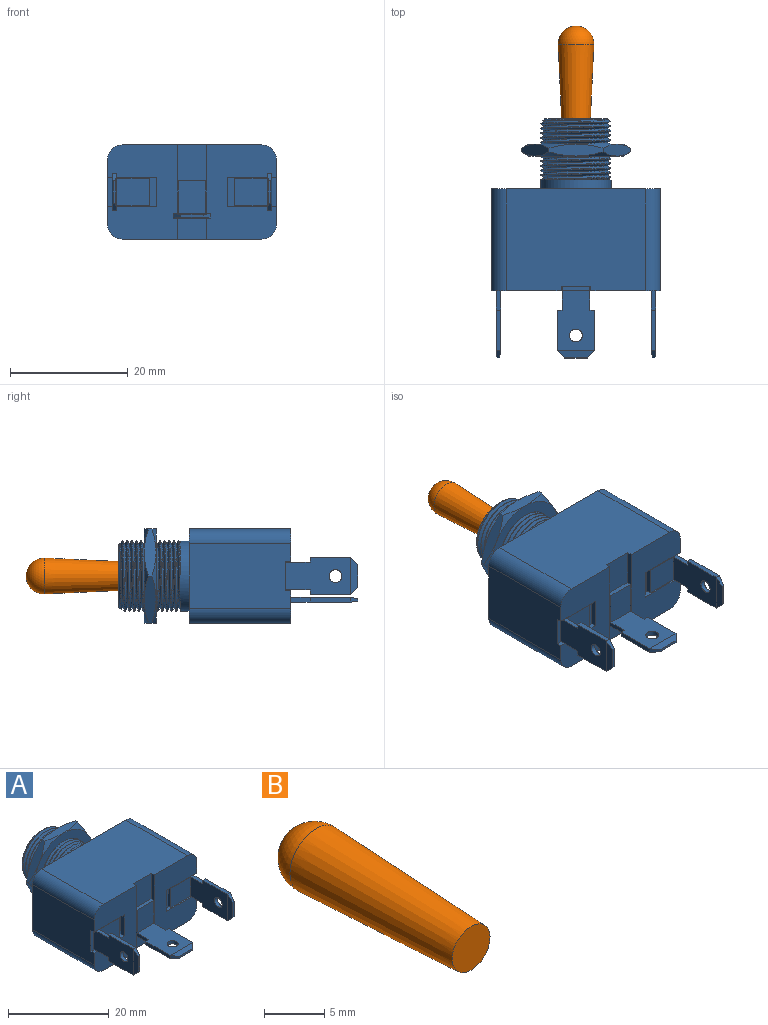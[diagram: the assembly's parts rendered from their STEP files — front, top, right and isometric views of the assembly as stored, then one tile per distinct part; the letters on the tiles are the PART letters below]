
ASSEMBLY  parts=2 mates=1
PART A: 155 faces, bbox 29.5x41.7x19.2 mm
  f0: cylinder r=5.95mm len=11.87mm, axis (0,1,0), area 2.4mm2, adj f6,f10,f12,f87
  f1: cylinder r=5.95mm len=0.9mm, axis (0,1,0), area 0mm2, adj f4,f11,f80
  f2: cylinder r=5.95mm len=11.91mm, axis (0,1,0), area 3.5mm2, adj f7,f11,f12,f36,f80
  f3: cylinder r=5.44mm len=4.26mm, axis (0,-1,0), area 0.4mm2, adj f5,f8,f11,f80
  f4: bspline ~11.99x11.99mm, area 11.2mm2, adj f1,f11,f12,f25,f80
  f5: bspline ~4.24x2.15mm, area 0mm2, adj f3,f11,f80
  f6: bspline ~11.99x11.99mm, area 15.3mm2, adj f0,f12,f26,f87
  f7: bspline ~11.99x11.99mm, area 20.1mm2, adj f2,f11,f12,f25,f80
  f8: bspline ~6x6mm, area 1.1mm2, adj f3,f11,f80
  f9: bspline ~11.99x11.99mm, area 5.4mm2, adj f12,f26,f87
  f10: bspline ~11.99x11.99mm, area 19.6mm2, adj f0,f11,f12,f27,f87
  f11: plane 10.42x0.95mm, normal (0,0,-1), area 6.8mm2, adj f1,f2,f3,f4,f5,f7,f8,f10
  f12: plane 10.42x0.95mm, normal (0,0,1), area 6.8mm2, adj f0,f2,f4,f6,f7,f9,f10,f14
  f13: cylinder r=5.95mm len=11.91mm, axis (0,1,0), area 59mm2, adj f11,f41,f50,f58,f67
  f14: cylinder r=5.95mm len=11.91mm, axis (0,1,0), area 3.5mm2, adj f11,f12,f40,f49
  f15: cylinder r=5.95mm len=11.91mm, axis (0,1,0), area 3.5mm2, adj f11,f12,f39,f48
  f16: cylinder r=5.95mm len=11.91mm, axis (0,1,0), area 3.5mm2, adj f11,f12,f38,f47
  f17: cylinder r=5.95mm len=11.91mm, axis (0,1,0), area 3.5mm2, adj f11,f12,f37,f46
  f18: cylinder r=5.95mm len=11.91mm, axis (0,1,0), area 3.5mm2, adj f11,f12,f35,f45
  f19: cylinder r=5.95mm len=11.91mm, axis (0,1,0), area 3.5mm2, adj f11,f12,f34,f44
  f20: cylinder r=5.95mm len=11.91mm, axis (0,1,0), area 3.5mm2, adj f11,f12,f33,f43
  f21: cylinder r=5.44mm len=10.88mm, axis (0,-1,0), area 3.2mm2, adj f11,f12,f33,f42
  f22: cylinder r=5.44mm len=10.88mm, axis (0,-1,0), area 3.2mm2, adj f11,f12,f34,f43
  f23: cylinder r=5.44mm len=10.88mm, axis (0,-1,0), area 3.2mm2, adj f11,f12,f35,f44
  f24: cylinder r=5.44mm len=10.88mm, axis (0,-1,0), area 3.2mm2, adj f11,f12,f36,f45
  f25: cylinder r=5.44mm len=10.88mm, axis (0,-1,0), area 3.2mm2, adj f4,f7,f11,f12
  f26: cylinder r=5.44mm len=10.88mm, axis (0,-1,0), area 2.7mm2, adj f6,f9,f12,f87
  f27: cylinder r=5.44mm len=10.88mm, axis (0,-1,0), area 3.2mm2, adj f10,f11,f12,f37
  f28: cylinder r=5.44mm len=10.88mm, axis (0,-1,0), area 3.2mm2, adj f11,f12,f38,f46
  f29: cylinder r=5.44mm len=10.88mm, axis (0,-1,0), area 3.2mm2, adj f11,f12,f39,f47
  f30: cylinder r=5.44mm len=10.88mm, axis (0,-1,0), area 3.2mm2, adj f11,f12,f40,f48
  f31: cylinder r=5.44mm len=10.88mm, axis (0,-1,0), area 3.2mm2, adj f11,f12,f41,f49
  f32: cylinder r=5.44mm len=2.83mm, axis (0,-1,0), area 0.1mm2, adj f11,f50,f58
  f33: bspline ~11.99x11.99mm, area 20.2mm2, adj f11,f12,f20,f21
  f34: bspline ~11.99x11.99mm, area 20.2mm2, adj f11,f12,f19,f22
  f35: bspline ~11.99x11.99mm, area 20.2mm2, adj f11,f12,f18,f23
  f36: bspline ~11.99x11.99mm, area 20.2mm2, adj f2,f11,f12,f24
  f37: bspline ~11.99x11.99mm, area 20.2mm2, adj f11,f12,f17,f27
  f38: bspline ~11.99x11.99mm, area 20.2mm2, adj f11,f12,f16,f28
  f39: bspline ~11.99x11.99mm, area 20.2mm2, adj f11,f12,f15,f29
  f40: bspline ~11.99x11.99mm, area 20.2mm2, adj f11,f12,f14,f30
  f41: bspline ~11.99x11.99mm, area 16.6mm2, adj f11,f12,f13,f31,f58
  f42: bspline ~11.99x11.99mm, area 20.1mm2, adj f11,f12,f21,f52,f56
  f43: bspline ~11.99x11.99mm, area 20.2mm2, adj f11,f12,f20,f22
  f44: bspline ~11.99x11.99mm, area 20.2mm2, adj f11,f12,f19,f23
  f45: bspline ~11.99x11.99mm, area 20.2mm2, adj f11,f12,f18,f24
  f46: bspline ~11.99x11.99mm, area 20.2mm2, adj f11,f12,f17,f28
  f47: bspline ~11.99x11.99mm, area 20.2mm2, adj f11,f12,f16,f29
  f48: bspline ~11.99x11.99mm, area 20.2mm2, adj f11,f12,f15,f30
  f49: bspline ~11.99x11.99mm, area 20.2mm2, adj f11,f12,f14,f31
  f50: bspline ~11.99x6mm, area 6.1mm2, adj f11,f13,f32,f58
  f51: cone r=5.35mm half-angle=45deg, axis (0,-1,0), area 13.3mm2, adj f11,f12,f53,f55,f57
  f52: cylinder r=5.95mm len=11.91mm, axis (0,1,0), area 2.9mm2, adj f12,f42,f54,f56
  f53: cylinder r=5.44mm len=10.88mm, axis (0,-1,0), area 3.1mm2, adj f11,f12,f51,f54,f55
  f54: bspline ~11.99x11.99mm, area 18.1mm2, adj f11,f12,f52,f53,f56
  f55: bspline ~11.84x11.84mm, area 7.7mm2, adj f12,f51,f53
  f56: cone r=5.35mm half-angle=45deg, axis (0,-1,0), area 2.5mm2, adj f11,f42,f52,f54
  f57: plane 10.7x10.63mm, normal (0,1,0), area 30.7mm2, adj f11,f12,f51,f68,f70
  f58: plane 12.23x12.23mm, normal (0,1,0), area 10.2mm2, adj f11,f12,f13,f32,f41,f50,f70
  f59: cylinder r=2.54mm len=17.27mm, axis (0,1,0), area 68.9mm2, adj f60,f66,f67,f145
  f60: plane 23.62x17.27mm, normal (0,0,1), area 404.1mm2, adj f59,f61,f67,f110,f145,f146,f153,f154
  f61: cylinder r=2.54mm len=17.27mm, axis (0,1,0), area 68.9mm2, adj f60,f62,f67,f146
  f62: plane 17.27x10.92mm, normal (-1,0,0), area 184.1mm2, adj f61,f63,f67,f127,f146,f147,f149
  f63: cylinder r=2.54mm len=17.27mm, axis (0,1,0), area 68.9mm2, adj f62,f64,f67,f146
  f64: plane 23.62x17.27mm, normal (0,0,-1), area 404.1mm2, adj f63,f65,f67,f110,f145,f146,f153,f154
  f65: cylinder r=2.54mm len=17.27mm, axis (0,1,0), area 68.9mm2, adj f64,f66,f67,f145
  f66: plane 17.27x10.92mm, normal (1,0,0), area 184.1mm2, adj f59,f65,f67,f144,f145,f150,f151
  f67: plane 28.7x16mm, normal (0,1,0), area 342.4mm2, adj f13,f59,f60,f61,f62,f63,f64,f65
  f68: cylinder r=4.32mm len=11.94mm, axis (0,1,0), area 323.9mm2, adj f57,f69
  f69: plane 8.64x8.64mm, normal (0,1,0), area 58.6mm2, adj f68
  f70: plane 10.41x1.78mm, normal (1,0,0), area 18.5mm2, adj f11,f12,f57,f58
  f71: cylinder r=5.44mm len=1.78mm, axis (0,-1,0), area 1.5mm2, adj f11,f12,f80,f87
  f72: plane 16x16mm, normal (0,1,0), area 86.5mm2, adj f80,f81,f82,f83,f84,f85,f86
  f73: plane 16x16mm, normal (0,-1,0), area 86.5mm2, adj f87,f88,f89,f90,f91,f92,f93
  f74: plane 8.76x5.38mm, normal (0.87,0,-0.5), area 14.2mm2, adj f75,f79,f82,f86,f88,f93
  f75: plane 10.01x2.8mm, normal (0,0,-1), area 14.2mm2, adj f74,f76,f85,f86,f92,f93
  f76: plane 8.76x5.38mm, normal (-0.87,0,-0.5), area 14.2mm2, adj f75,f77,f84,f85,f91,f92
  f77: plane 8.76x5.38mm, normal (-0.87,0,0.5), area 14.2mm2, adj f76,f78,f83,f84,f90,f91
  f78: plane 10.01x2.8mm, normal (0,0,1), area 14.2mm2, adj f77,f79,f81,f83,f89,f90
  f79: plane 8.76x5.38mm, normal (0.87,0,0.5), area 14.2mm2, adj f74,f78,f81,f82,f88,f89
  f80: cone r=6.04mm half-angle=45deg, axis (0,1,0), area 18.2mm2, adj f1,f2,f3,f4,f5,f7,f8,f11
  f81: cone r=9.24mm half-angle=60deg, axis (0,-1,0), area 6.3mm2, adj f72,f78,f79
  f82: cone r=9.24mm half-angle=60deg, axis (0,-1,0), area 6.3mm2, adj f72,f74,f79
  f83: cone r=9.24mm half-angle=60deg, axis (0,-1,0), area 6.3mm2, adj f72,f77,f78
  f84: cone r=9.24mm half-angle=60deg, axis (0,-1,0), area 6.3mm2, adj f72,f76,f77
  f85: cone r=9.24mm half-angle=60deg, axis (0,-1,0), area 6.3mm2, adj f72,f75,f76
  f86: cone r=9.24mm half-angle=60deg, axis (0,-1,0), area 6.3mm2, adj f72,f74,f75
  f87: cone r=5.44mm half-angle=45deg, axis (0,-1,0), area 18.7mm2, adj f0,f6,f9,f10,f11,f12,f26,f71
  f88: cone r=8mm half-angle=60deg, axis (0,1,0), area 6.3mm2, adj f73,f74,f79
  f89: cone r=8mm half-angle=60deg, axis (0,1,0), area 6.3mm2, adj f73,f78,f79
  f90: cone r=8mm half-angle=60deg, axis (0,1,0), area 6.3mm2, adj f73,f77,f78
  f91: cone r=8mm half-angle=60deg, axis (0,1,0), area 6.3mm2, adj f73,f76,f77
  f92: cone r=8mm half-angle=60deg, axis (0,1,0), area 6.3mm2, adj f73,f75,f76
  f93: cone r=8mm half-angle=60deg, axis (0,1,0), area 6.3mm2, adj f73,f74,f75
  f94: plane 10.92x6.35mm, normal (0,0,-1), area 58.9mm2, adj f95,f97,f100,f101,f103,f104,f105,f108
  f95: plane 6.35x4.06mm, normal (1,0,0), area 7.6mm2, adj f94,f96,f98,f99,f104,f110
  f96: plane 4.7x0.79mm, normal (0,0,1), area 3.7mm2, adj f95,f97,f98,f110
  f97: plane 6.35x4.06mm, normal (-1,0,0), area 7.6mm2, adj f94,f96,f98,f99,f100,f110
  f98: plane 5.56x4.7mm, normal (0,-1,0), area 26.1mm2, adj f95,f96,f97,f99
  f99: plane 10.13x6.35mm, normal (0,0,1), area 55.2mm2, adj f95,f97,f98,f100,f101,f103,f104,f105
  f100: plane 0.83x0.79mm, normal (0,1,0), area 0.7mm2, adj f94,f97,f99,f101
  f101: plane 6.86x0.79mm, normal (-1,0,0), area 5.4mm2, adj f94,f99,f100,f107
  f102: plane 3.81x0.41mm, normal (0,-1,0), area 1.6mm2, adj f106,f107,f108,f109
  f103: plane 6.86x0.79mm, normal (1,0,0), area 5.4mm2, adj f94,f99,f104,f106
  f104: plane 0.83x0.79mm, normal (0,1,0), area 0.7mm2, adj f94,f95,f99,f103
  f105: cylinder r=1.09mm len=2.18mm, axis (0,0,-1), area 5.4mm2, adj f94,f99
  f106: plane 1.27x1.27mm, normal (0.71,-0.71,0), area 1.1mm2, adj f102,f103,f108,f109
  f107: plane 1.27x1.27mm, normal (-0.71,-0.71,0), area 1.1mm2, adj f101,f102,f108,f109
  f108: plane 6.35x1.27mm, normal (0,-0.15,-0.99), area 6.5mm2, adj f94,f102,f106,f107
  f109: plane 6.35x1.27mm, normal (0,-0.15,0.99), area 6.5mm2, adj f99,f102,f106,f107
  f110: plane 16x5.08mm, normal (0,-1,0), area 51.5mm2, adj f60,f64,f94,f95,f96,f97,f153,f154
  f111: plane 4.7x0.79mm, normal (1,0,0), area 3.7mm2, adj f112,f114,f115,f127
  f112: plane 6.35x4.19mm, normal (0,0,-1), area 7.7mm2, adj f111,f113,f115,f116,f117,f127
  f113: plane 11.05x6.35mm, normal (-1,0,0), area 59.5mm2, adj f112,f114,f117,f118,f120,f121,f122,f126
  f114: plane 6.35x4.19mm, normal (0,0,1), area 7.7mm2, adj f111,f113,f115,f116,f121,f127
  f115: plane 5.56x4.7mm, normal (0,-1,0), area 26.1mm2, adj f111,f112,f114,f116
  f116: plane 10.26x6.35mm, normal (1,0,0), area 55.8mm2, adj f112,f114,f115,f117,f118,f120,f121,f122
  f117: plane 0.83x0.79mm, normal (0,1,0), area 0.7mm2, adj f112,f113,f116,f118
  f118: plane 6.86x0.79mm, normal (0,0,-1), area 5.4mm2, adj f113,f116,f117,f123
  f119: plane 3.81x0.41mm, normal (0,-1,0), area 1.6mm2, adj f123,f124,f125,f126
  f120: plane 6.86x0.79mm, normal (0,0,1), area 5.4mm2, adj f113,f116,f121,f124
  f121: plane 0.83x0.79mm, normal (0,1,0), area 0.7mm2, adj f113,f114,f116,f120
  f122: cylinder r=1.09mm len=2.18mm, axis (-1,0,0), area 5.4mm2, adj f113,f116
  f123: plane 1.27x1.27mm, normal (0,-0.71,-0.71), area 1.1mm2, adj f118,f119,f125,f126
  f124: plane 1.27x1.27mm, normal (0,-0.71,0.71), area 1.1mm2, adj f119,f120,f125,f126
  f125: plane 6.35x1.27mm, normal (0.99,-0.15,0), area 6.5mm2, adj f116,f119,f123,f124
  f126: plane 6.35x1.27mm, normal (-0.99,-0.15,0), area 6.5mm2, adj f113,f119,f123,f124
  f127: plane 8.38x5.08mm, normal (0,-1,0), area 12.7mm2, adj f62,f111,f112,f113,f114,f147,f148,f149
  f128: plane 4.7x0.79mm, normal (-1,0,0), area 3.7mm2, adj f129,f131,f132,f144
  f129: plane 6.35x4.19mm, normal (0,0,-1), area 7.7mm2, adj f128,f130,f132,f133,f134,f144
  f130: plane 11.05x6.35mm, normal (1,0,0), area 59.5mm2, adj f129,f131,f134,f135,f137,f138,f139,f143
  f131: plane 6.35x4.19mm, normal (0,0,1), area 7.7mm2, adj f128,f130,f132,f133,f138,f144
  f132: plane 5.56x4.7mm, normal (0,-1,0), area 26.1mm2, adj f128,f129,f131,f133
  f133: plane 10.26x6.35mm, normal (-1,0,0), area 55.8mm2, adj f129,f131,f132,f134,f135,f137,f138,f139
  f134: plane 0.83x0.79mm, normal (0,1,0), area 0.7mm2, adj f129,f130,f133,f135
  f135: plane 6.86x0.79mm, normal (0,0,-1), area 5.4mm2, adj f130,f133,f134,f140
  f136: plane 3.81x0.41mm, normal (0,-1,0), area 1.6mm2, adj f140,f141,f142,f143
  f137: plane 6.86x0.79mm, normal (0,0,1), area 5.4mm2, adj f130,f133,f138,f141
  f138: plane 0.83x0.79mm, normal (0,1,0), area 0.7mm2, adj f130,f131,f133,f137
  f139: cylinder r=1.09mm len=2.18mm, axis (1,0,0), area 5.4mm2, adj f130,f133
  f140: plane 1.27x1.27mm, normal (0,-0.71,-0.71), area 1.1mm2, adj f135,f136,f142,f143
  f141: plane 1.27x1.27mm, normal (0,-0.71,0.71), area 1.1mm2, adj f136,f137,f142,f143
  f142: plane 6.35x1.27mm, normal (-0.99,-0.15,0), area 6.5mm2, adj f133,f136,f140,f141
  f143: plane 6.35x1.27mm, normal (0.99,-0.15,0), area 6.5mm2, adj f130,f136,f140,f141
  f144: plane 8.38x5.08mm, normal (0,-1,0), area 12.7mm2, adj f66,f128,f129,f130,f131,f150,f151,f152
  f145: plane 16x11.81mm, normal (0,-1,0), area 143.7mm2, adj f59,f60,f64,f65,f66,f150,f151,f152
  f146: plane 16x11.81mm, normal (0,-1,0), area 143.7mm2, adj f60,f61,f62,f63,f64,f147,f148,f149
  f147: plane 8.38x0.89mm, normal (0,0,-1), area 7.5mm2, adj f62,f127,f146,f148
  f148: plane 5.08x0.89mm, normal (-1,0,0), area 4.5mm2, adj f127,f146,f147,f149
  f149: plane 8.38x0.89mm, normal (0,0,1), area 7.5mm2, adj f62,f127,f146,f148
  f150: plane 8.38x0.89mm, normal (0,0,-1), area 7.5mm2, adj f66,f144,f145,f152
  f151: plane 8.38x0.89mm, normal (0,0,1), area 7.5mm2, adj f66,f144,f145,f152
  f152: plane 5.08x0.89mm, normal (1,0,0), area 4.5mm2, adj f144,f145,f150,f151
  f153: plane 16x0.76mm, normal (-1,0,0), area 12.2mm2, adj f60,f64,f110,f145
  f154: plane 16x0.76mm, normal (1,0,0), area 12.2mm2, adj f60,f64,f110,f146
PART B: 3 faces, bbox 6.1x21.3x6.1 mm
  f0: sphere r=3.05mm, area 61mm2, adj f1
  f1: cone r=3.04mm half-angle=2.6deg, axis (0,1,0), area 300.2mm2, adj f0,f2
  f2: plane 4.43x4.43mm, normal (0,-1,0), area 15.4mm2, adj f1
PLACE A t=(-129.8,-142.59,-119.4)mm
PLACE B t=(-129.8,-141.06,-119.4)mm
MATE fastened A.f68 <-> B.f1  axis (0,1,0) through (-129.8,-142.59,-119.4)mm
